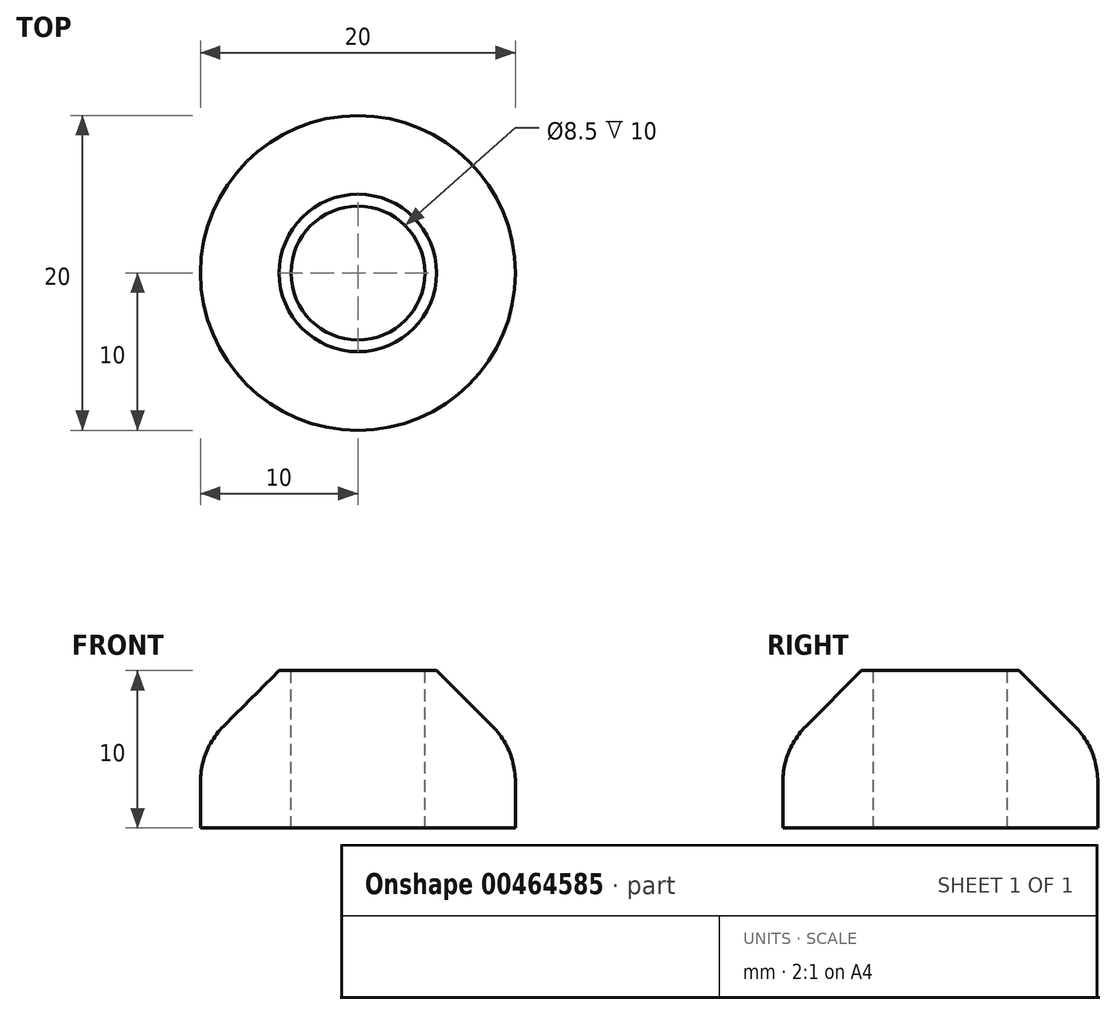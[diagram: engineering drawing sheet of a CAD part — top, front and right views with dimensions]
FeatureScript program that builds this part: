
annotation { "Feature Type Name" : "Feature", "Feature Type Description" : "" }
export const myFeature = defineFeature(function(context is Context, id is Id, definition is map)
    precondition{}
    {
        {
            var Q0;
            Q0=qCreatedBy(makeId("Top.planeOp"),FACE);
            var sketch = newSketch(context, id + "F0", { "sketchPlane" : qUnion([Q0])});
            skCircle(sketch, "E0", {"center": v(0, 0) * mm, "radius": 10 * mm});
            skSolve(sketch);
        }
        {
            var Q0;
            Q0 = qSketchRegion(id + "F0", true);
            extrude(context, id + "F1", {"entities" : qUnion([Q0]), "depth" : 10 * mm, "offsetDistance" : 25 * mm});
        }
        {
            var Q0;
            Q0=makeQuery(id+"F1.opExtrude","CAP_FACE",FACE,{"disambiguationData":[OSD([sQuery(id+"F0.wireOp",EDGE,"E0")])],"isStart":false});
            var sketch = newSketch(context, id + "F2", { "sketchPlane" : qUnion([Q0])});
            skCircle(sketch, "E1", {"center": v(0, 0) * mm, "radius": 4.25 * mm});
            skSolve(sketch);
        }
        {
            var Q0;
            Q0 = qSketchRegion(id + "F2", true);
            extrude(context, id + "F3", {"entities" : qUnion([Q0]), "operationType" : NewBodyOperationType.REMOVE, "endBound" : BoundingType.THROUGH_ALL, "oppositeDirection" : true, "depth" : 25 * mm, "offsetDistance" : 25 * mm});
        }
        {
            var Q0;
            Q0=makeQuery(id+"F1.opExtrude","CAP_EDGE",EDGE,{"disambiguationData":[OSD([sQuery(id+"F0.wireOp",EDGE,"E0")])],"isStart":false});
            chamfer(context, id + "F4", {"entities" : qUnion([Q0]), "width" : 5 * mm, "tangentPropagation" : true});
        }
        {
            var Q0;
            {var subQ0=sQuery(id+"F0.wireOp",EDGE,"E0");Q0=makeQuery(id+"F4.opChamfer","BLEND_EDGE",EDGE,{"blendedFrom":[makeQuery(id+"F1.opExtrude","CAP_EDGE",EDGE,{"disambiguationData":[OSD([subQ0])],"isStart":false}),makeQuery(id+"F1.opExtrude","SWEPT_FACE",FACE,{"disambiguationData":[OSD([subQ0])]})],"blendedInto":[makeQuery(id+"F1.opExtrude","SWEPT_FACE",FACE,{"disambiguationData":[OSD([subQ0])]})]});}
            fillet(context, id + "F5", {"entities" : qUnion([Q0]), "radius" : 5 * mm, "tangentPropagation" : true, "allowEdgeOverflow" : false});
        }
    });
